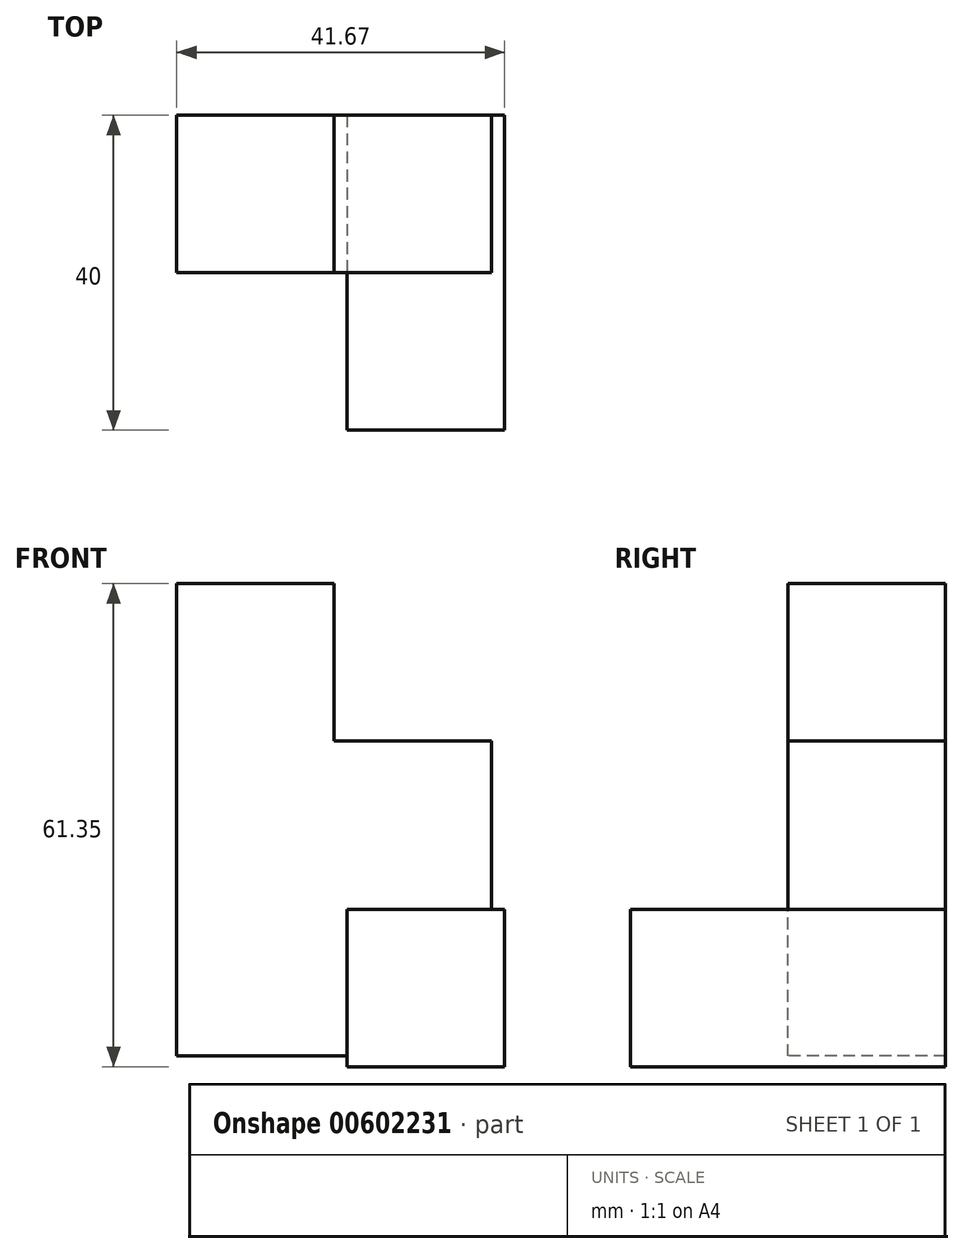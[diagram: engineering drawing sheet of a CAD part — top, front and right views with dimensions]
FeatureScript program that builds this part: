
annotation { "Feature Type Name" : "Feature", "Feature Type Description" : "" }
export const myFeature = defineFeature(function(context is Context, id is Id, definition is map)
    precondition{}
    {
        {
            var Q0;
            Q0=qCreatedBy(makeId("Front.planeOp"),FACE);
            var sketch = newSketch(context, id + "F0", { "sketchPlane" : qUnion([Q0])});
            skLineSegment(sketch, "E0", {"start": v(-36.86, 34.24) * mm, "end": v(-16.86, 34.24) * mm});
            skLineSegment(sketch, "E1", {"start": v(-16.86, 34.24) * mm, "end": v(-16.86, 14.24) * mm});
            skLineSegment(sketch, "E2", {"start": v(-16.86, 14.24) * mm, "end": v(3.14, 14.24) * mm});
            skLineSegment(sketch, "E3", {"start": v(3.14, 14.24) * mm, "end": v(3.14, -25.76) * mm});
            skLineSegment(sketch, "E4", {"start": v(3.14, -25.76) * mm, "end": v(-36.86, -25.76) * mm});
            skLineSegment(sketch, "E5", {"start": v(-36.86, -25.76) * mm, "end": v(-36.86, 34.24) * mm});
            skSolve(sketch);
        }
        {
            var Q0;
            Q0 = qSketchRegion(id + "F0", true);
            extrude(context, id + "F1", {"entities" : qUnion([Q0]), "depth" : 20 * mm, "offsetDistance" : 25 * mm});
        }
        {
            var Q0;
            Q0=qCreatedBy(makeId("Front.planeOp"),FACE);
            var sketch = newSketch(context, id + "F2", { "sketchPlane" : qUnion([Q0])});
            skLineSegment(sketch, "E6", {"start": v(-15.19, -7.11) * mm, "end": v(-15.19, -27.11) * mm});
            skLineSegment(sketch, "E7", {"start": v(-15.19, -27.11) * mm, "end": v(4.81, -27.11) * mm});
            skLineSegment(sketch, "E8", {"start": v(4.81, -27.11) * mm, "end": v(4.81, -7.11) * mm});
            skLineSegment(sketch, "E9", {"start": v(4.81, -7.11) * mm, "end": v(-15.19, -7.11) * mm});
            skSolve(sketch);
        }
        {
            var Q0;
            Q0 = qSketchRegion(id + "F2", true);
            extrude(context, id + "F3", {"entities" : qUnion([Q0]), "operationType" : NewBodyOperationType.ADD, "depth" : 40 * mm, "offsetDistance" : 25 * mm});
        }
    });
